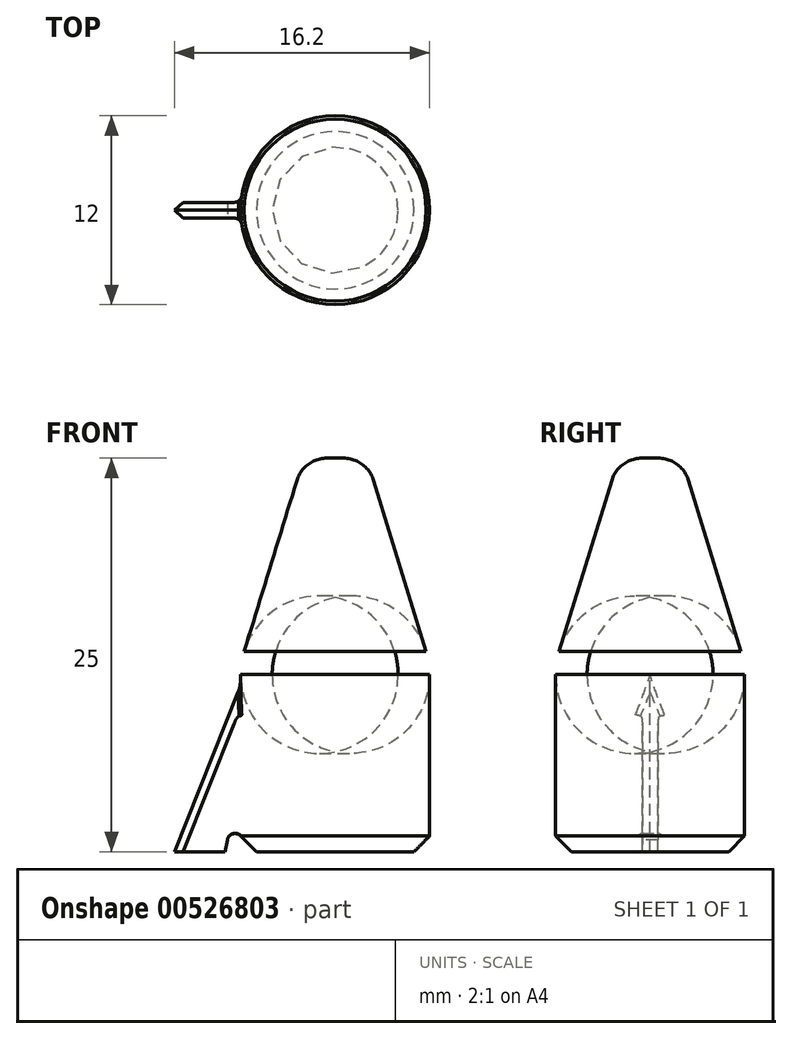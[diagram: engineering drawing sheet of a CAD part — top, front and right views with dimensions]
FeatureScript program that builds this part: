
annotation { "Feature Type Name" : "Feature", "Feature Type Description" : "" }
export const myFeature = defineFeature(function(context is Context, id is Id, definition is map)
    precondition{}
    {
        {
            var Q0;
            Q0=qCreatedBy(makeId("Front.planeOp"),FACE);
            var sketch = newSketch(context, id + "F0", { "sketchPlane" : qUnion([Q0])});
            skLineSegment(sketch, "E0.bottom", {"start": v(0, 0) * mm, "end": v(-6, 0) * mm});
            skLineSegment(sketch, "E0.top", {"start": v(0, 25) * mm, "end": v(-2, 25) * mm});
            skLineSegment(sketch, "E0.left", {"start": v(0, 0) * mm, "end": v(0, 25) * mm});
            skLineSegment(sketch, "E1", {"start": v(-6, 0) * mm, "end": v(-6, 12) * mm});
            skLineSegment(sketch, "E2", {"start": v(-6, 12) * mm, "end": v(-6, 12) * mm});
            skLineSegment(sketch, "E3", {"start": v(-6, 12) * mm, "end": v(-2, 25) * mm});
            skLineSegment(sketch, "E4", {"start": v(0, 49.31) * mm, "end": v(0, -9.7) * mm, "construction": true});
            skSolve(sketch);
        }
        {
            var Q0;
            Q0=makeQuery(id+"F0.imprint","IMPRINT",FACE,{"disambiguationData":[TD([[makeQuery(id+"F0.imprint","IMPRINT",EDGE,{"derivedFrom":sQuery(id+"F0.wireOp",EDGE,"E0.bottom")}),-1.0]])]});
            var Q1;
            Q1=sQuery(id+"F0.wireOp",EDGE,"E4");
            revolve(context, id + "F1", {"entities" : qUnion([Q0]), "axis" : qUnion([Q1]), "revolveType" : RevolveType.FULL});
        }
        {
            var Q0;
            Q0=makeQuery(id+"F1.opRevolve","SWEPT_EDGE",EDGE,{"disambiguationData":[OSD([sQuery(id+"F0.wireOp",EDGE,"E0.top"),sQuery(id+"F0.wireOp",EDGE,"E3")])]});
            fillet(context, id + "F2", {"entities" : qUnion([Q0]), "radius" : 2 * mm, "tangentPropagation" : true, "allowEdgeOverflow" : false});
        }
        {
            var Q0;
            Q0=makeQuery(id+"F1.opRevolve","SWEPT_EDGE",EDGE,{"disambiguationData":[OSD([sQuery(id+"F0.wireOp",EDGE,"E1"),sQuery(id+"F0.wireOp",EDGE,"E3")])]});
            fillet(context, id + "F3", {"entities" : qUnion([Q0]), "radius" : 5 * mm, "tangentPropagation" : true, "allowEdgeOverflow" : false});
        }
        {
            var Q0;
            Q0=makeQuery(id+"F1.opRevolve","SWEPT_EDGE",EDGE,{"disambiguationData":[OSD([sQuery(id+"F0.wireOp",EDGE,"E0.bottom"),sQuery(id+"F0.wireOp",EDGE,"E1")])]});
            chamfer(context, id + "F4", {"entities" : qUnion([Q0]), "width" : 1 * mm, "tangentPropagation" : true});
        }
        {
            var Q0;
            Q0=qCreatedBy(makeId("Front.planeOp"),FACE);
            var sketch = newSketch(context, id + "F5", { "sketchPlane" : qUnion([Q0])});
            skLineSegment(sketch, "E5", {"start": v(-5.8, 11.05) * mm, "end": v(-10.2, 0) * mm});
            skLineSegment(sketch, "E6", {"start": v(-10.2, 0) * mm, "end": v(-7, 0) * mm});
            skLineSegment(sketch, "E7", {"start": v(-7, 0) * mm, "end": v(-5.8, 6.05) * mm});
            skLineSegment(sketch, "E8", {"start": v(-5.8, 11.05) * mm, "end": v(-5.8, 6.05) * mm});
            skSolve(sketch);
        }
        {
            var Q0;
            Q0=makeQuery(id+"F5.imprint","IMPRINT",FACE,{"disambiguationData":[TD([[makeQuery(id+"F5.imprint","IMPRINT",EDGE,{"derivedFrom":sQuery(id+"F5.wireOp",EDGE,"E5")}),1.0]])]});
            extrude(context, id + "F6", {"entities" : qUnion([Q0]), "operationType" : NewBodyOperationType.ADD, "endBound" : BoundingType.SYMMETRIC, "depth" : 1 * mm, "offsetDistance" : 25 * mm});
        }
        {
            var Q0;
            Q0=makeQuery(id+"F6.opExtrude","CAP_EDGE",EDGE,{"disambiguationData":[OSD([sQuery(id+"F5.wireOp",EDGE,"E5")])],"isStart":false});
            var Q1;
            Q1=makeQuery(id+"F6.opExtrude","CAP_EDGE",EDGE,{"disambiguationData":[OSD([sQuery(id+"F5.wireOp",EDGE,"E5")])],"isStart":true});
            chamfer(context, id + "F7", {"entities" : qUnion([Q0, Q1]), "width" : .5 * mm, "tangentPropagation" : true});
        }
        {
            var Q0;
            Q0=makeQuery(id+"F6.boolean.opBoolean","INTERSECT",EDGE,{"derivedFrom":[makeQuery(id+"F1.opRevolve","SWEPT_FACE",FACE,{"disambiguationData":[OSD([sQuery(id+"F0.wireOp",EDGE,"E1")])]}),makeQuery(id+"F6.opExtrude","CAP_FACE",FACE,{"disambiguationData":[OSD([sQuery(id+"F5.wireOp",EDGE,"E5"),sQuery(id+"F5.wireOp",EDGE,"E6"),sQuery(id+"F5.wireOp",EDGE,"E7"),sQuery(id+"F5.wireOp",EDGE,"E8")])],"isStart":false})]});
            var Q1;
            Q1=makeQuery(id+"F7.opChamfer","BLEND_EDGE",EDGE,{"blendedFrom":[makeQuery(id+"F6.opExtrude","CAP_EDGE",EDGE,{"disambiguationData":[OSD([sQuery(id+"F5.wireOp",EDGE,"E5")])],"isStart":false}),makeQuery(id+"F1.opRevolve","SWEPT_FACE",FACE,{"disambiguationData":[OSD([sQuery(id+"F0.wireOp",EDGE,"E1")])]})],"blendedInto":[makeQuery(id+"F1.opRevolve","SWEPT_FACE",FACE,{"disambiguationData":[OSD([sQuery(id+"F0.wireOp",EDGE,"E1")])]})]});
            var Q2;
            Q2=makeQuery(id+"F7.opChamfer","BLEND_EDGE",EDGE,{"blendedFrom":[makeQuery(id+"F6.opExtrude","CAP_EDGE",EDGE,{"disambiguationData":[OSD([sQuery(id+"F5.wireOp",EDGE,"E5")])],"isStart":true}),makeQuery(id+"F1.opRevolve","SWEPT_FACE",FACE,{"disambiguationData":[OSD([sQuery(id+"F0.wireOp",EDGE,"E1")])]})],"blendedInto":[makeQuery(id+"F1.opRevolve","SWEPT_FACE",FACE,{"disambiguationData":[OSD([sQuery(id+"F0.wireOp",EDGE,"E1")])]})]});
            var Q3;
            Q3=makeQuery(id+"F6.boolean.opBoolean","INTERSECT",EDGE,{"derivedFrom":[makeQuery(id+"F1.opRevolve","SWEPT_FACE",FACE,{"disambiguationData":[OSD([sQuery(id+"F0.wireOp",EDGE,"E1")])]}),makeQuery(id+"F6.opExtrude","CAP_FACE",FACE,{"disambiguationData":[OSD([sQuery(id+"F5.wireOp",EDGE,"E5"),sQuery(id+"F5.wireOp",EDGE,"E6"),sQuery(id+"F5.wireOp",EDGE,"E7"),sQuery(id+"F5.wireOp",EDGE,"E8")])],"isStart":true})]});
            var Q4;
            Q4=makeQuery(id+"F6.boolean.opBoolean","INTERSECT",EDGE,{"derivedFrom":[makeQuery(id+"F1.opRevolve","SWEPT_FACE",FACE,{"disambiguationData":[OSD([sQuery(id+"F0.wireOp",EDGE,"E1")])]}),makeQuery(id+"F6.opExtrude","SWEPT_FACE",FACE,{"disambiguationData":[OSD([sQuery(id+"F5.wireOp",EDGE,"E7")])]})]});
            fillet(context, id + "F8", {"entities" : qUnion([Q0, Q1, Q2, Q3, Q4]), "radius" : .5 * mm, "tangentPropagation" : true, "allowEdgeOverflow" : false});
        }
    });
